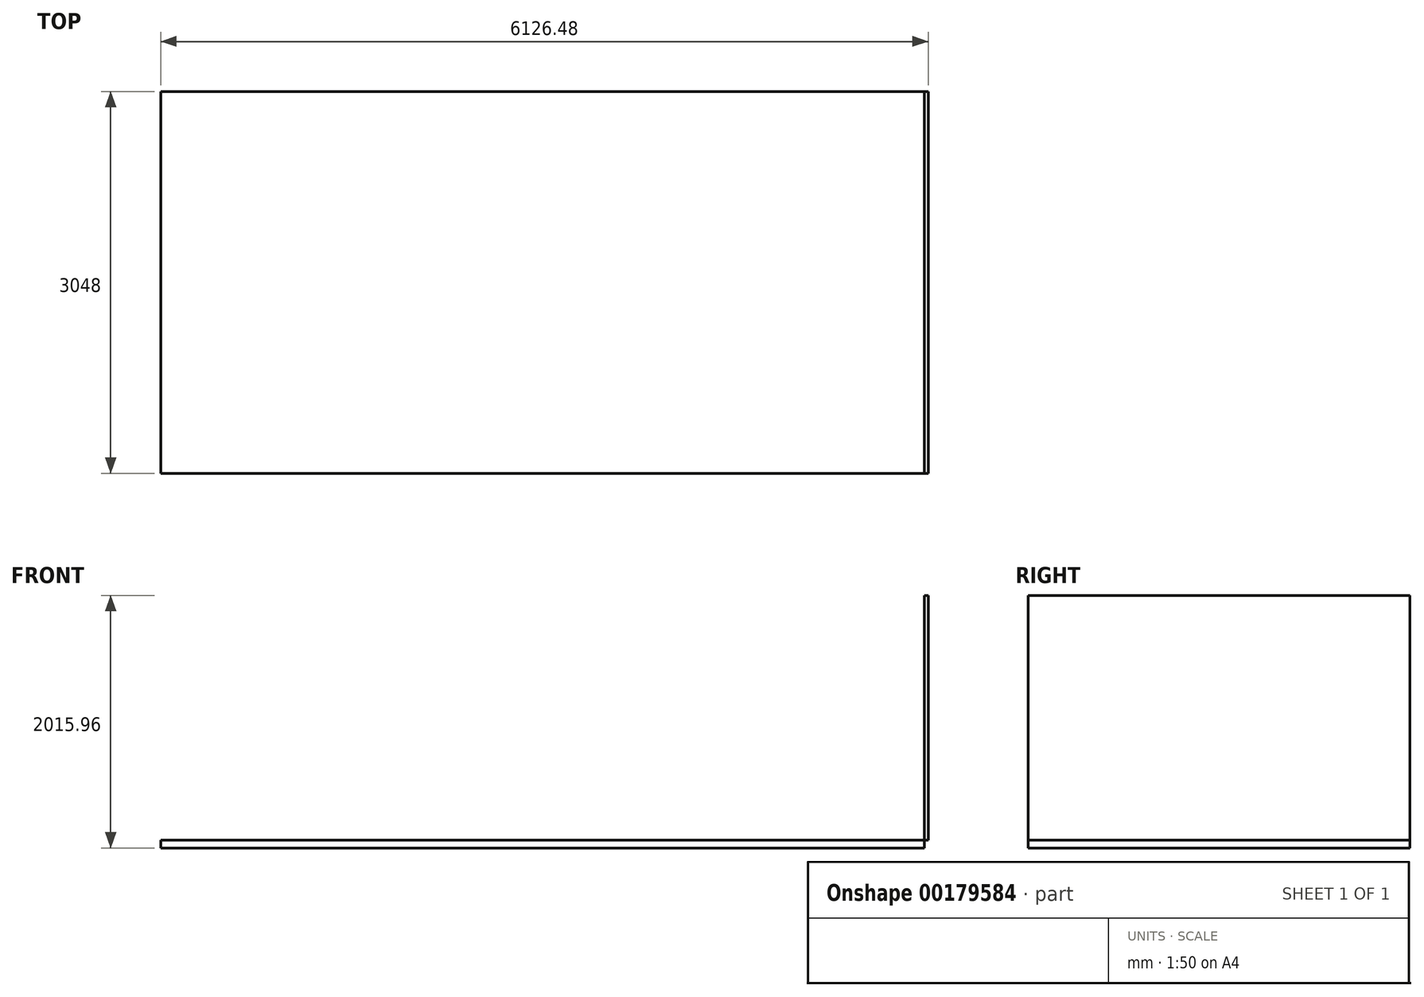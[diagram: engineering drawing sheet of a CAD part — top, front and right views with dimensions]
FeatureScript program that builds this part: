
annotation { "Feature Type Name" : "Feature", "Feature Type Description" : "" }
export const myFeature = defineFeature(function(context is Context, id is Id, definition is map)
    precondition{}
    {
        {
            var Q0;
            Q0=qCreatedBy(makeId("Top.planeOp"),FACE);
            var sketch = newSketch(context, id + "F0", { "sketchPlane" : qUnion([Q0])});
            skLineSegment(sketch, "E0.bottom", {"start": v(-3048, 1524) * mm, "end": v(3048, 1524) * mm});
            skLineSegment(sketch, "E0.top", {"start": v(-3048, -1524) * mm, "end": v(3048, -1524) * mm});
            skLineSegment(sketch, "E0.left", {"start": v(-3048, 1524) * mm, "end": v(-3048, -1524) * mm});
            skLineSegment(sketch, "E0.right", {"start": v(3048, 1524) * mm, "end": v(3048, -1524) * mm});
            skPoint(sketch, "E0.middle", {"position": v(0, 0) * mm});
            skSolve(sketch);
        }
        {
            var Q0;
            Q0=makeQuery(id+"F0.imprint","IMPRINT",FACE,{"disambiguationData":[TD([[makeQuery(id+"F0.imprint","IMPRINT",EDGE,{"derivedFrom":sQuery(id+"F0.wireOp",EDGE,"E0.bottom")}),-1.0]])]});
            extrude(context, id + "F1", {"entities" : qUnion([Q0]), "depth" : 60.96 * mm});
        }
        {
            var Q0;
            Q0=makeQuery(id+"F1.opExtrude","SWEPT_FACE",FACE,{"disambiguationData":[OSD([sQuery(id+"F0.wireOp",EDGE,"E0.right")])]});
            var sketch = newSketch(context, id + "F2", { "sketchPlane" : qUnion([Q0])});
            skLineSegment(sketch, "E1.bottom", {"start": v(-1524, 60.96) * mm, "end": v(1524, 60.96) * mm});
            skLineSegment(sketch, "E1.top", {"start": v(-1524, 60.96) * mm, "end": v(1524, 60.96) * mm});
            skLineSegment(sketch, "E1.left", {"start": v(-1524, 60.96) * mm, "end": v(-1524, 60.96) * mm});
            skLineSegment(sketch, "E1.right", {"start": v(1524, 60.96) * mm, "end": v(1524, 60.96) * mm});
            skLineSegment(sketch, "E2.bottom", {"start": v(1524, 2015.96) * mm, "end": v(-1524, 2015.96) * mm});
            skLineSegment(sketch, "E2.top", {"start": v(1524, 60.96) * mm, "end": v(-1524, 60.96) * mm});
            skLineSegment(sketch, "E2.left", {"start": v(1524, 2015.96) * mm, "end": v(1524, 60.96) * mm});
            skLineSegment(sketch, "E2.right", {"start": v(-1524, 2015.96) * mm, "end": v(-1524, 60.96) * mm});
            skSolve(sketch);
        }
        {
            var Q0;
            Q0=makeQuery(id+"F2.imprint","IMPRINT",FACE,{"disambiguationData":[TD([[makeQuery(id+"F2.imprint","IMPRINT",EDGE,{"derivedFrom":sQuery(id+"F2.wireOp",EDGE,"E2.bottom")}),1.0]])]});
            extrude(context, id + "F3", {"entities" : qUnion([Q0]), "depth" : 30.48 * mm});
        }
    });
